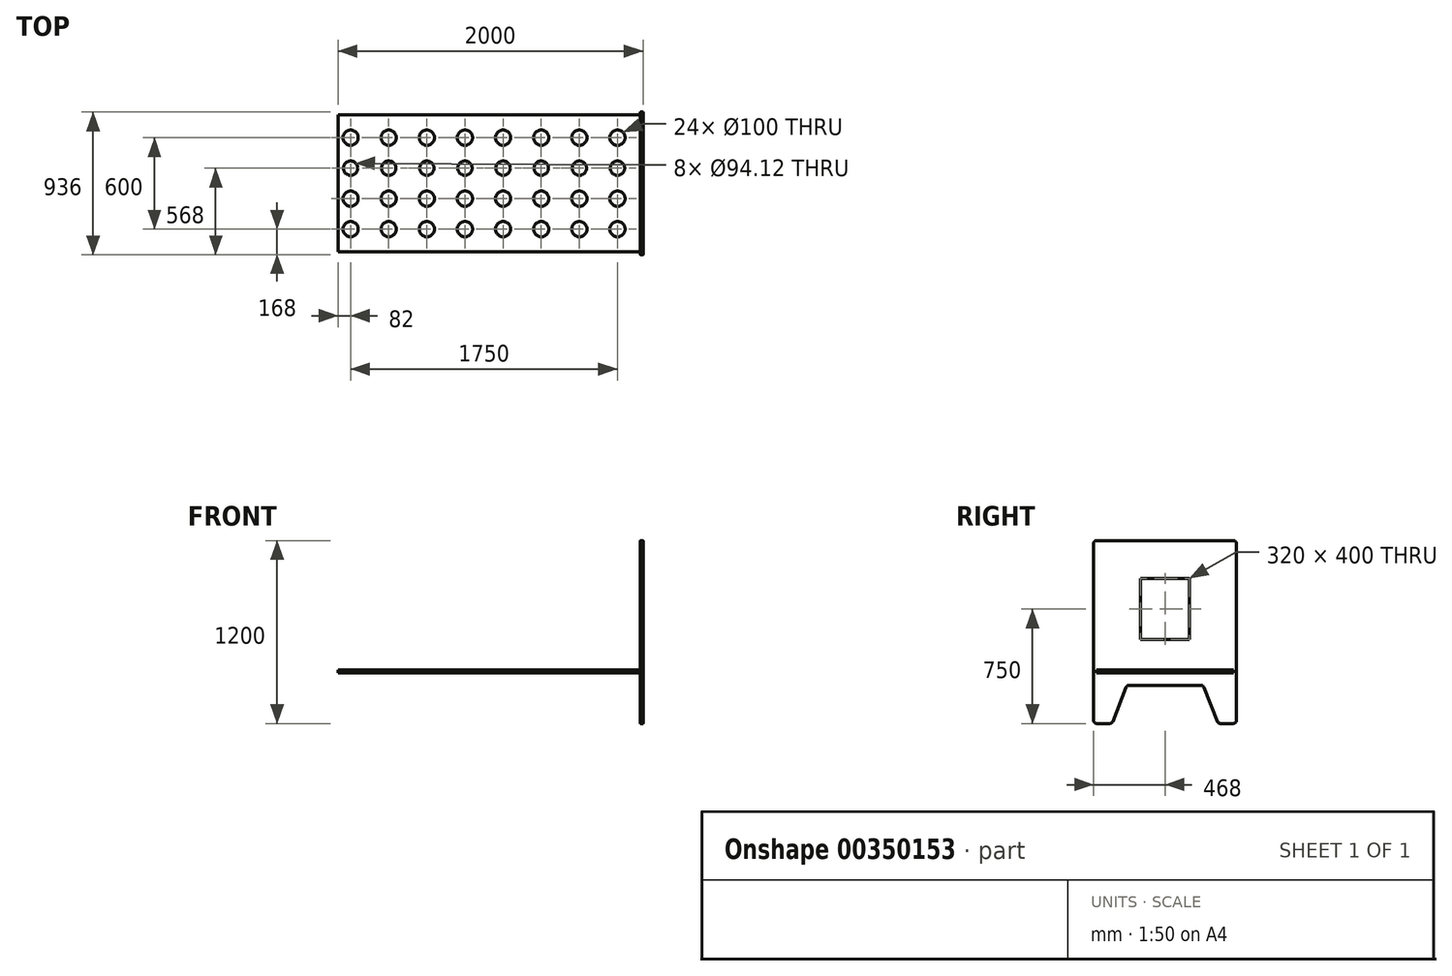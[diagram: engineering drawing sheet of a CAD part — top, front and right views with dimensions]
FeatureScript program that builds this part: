
annotation { "Feature Type Name" : "Feature", "Feature Type Description" : "" }
export const myFeature = defineFeature(function(context is Context, id is Id, definition is map)
    precondition{}
    {
        {
            var Q0;
            Q0=qCreatedBy(makeId("Right.planeOp"),FACE);
            var sketch = newSketch(context, id + "F0", { "sketchPlane" : qUnion([Q0])});
            skLineSegment(sketch, "E0.bottom", {"start": v(-468, 600) * mm, "end": v(468, 600) * mm});
            skLineSegment(sketch, "E0.top", {"start": v(-468, -600) * mm, "end": v(-348, -600) * mm});
            skLineSegment(sketch, "E0.left", {"start": v(-468, 600) * mm, "end": v(-468, -600) * mm});
            skLineSegment(sketch, "E0.right", {"start": v(468, 600) * mm, "end": v(468, -600) * mm});
            skPoint(sketch, "E0.middle", {"position": v(0, 0) * mm});
            skLineSegment(sketch, "E1", {"start": v(-348, -600) * mm, "end": v(-250, -350) * mm});
            skLineSegment(sketch, "E2", {"start": v(-250, -350) * mm, "end": v(250, -350) * mm});
            skLineSegment(sketch, "E3", {"start": v(250, -350) * mm, "end": v(348, -600) * mm});
            skLineSegment(sketch, "E4.trimOffspring", {"start": v(348, -600) * mm, "end": v(468, -600) * mm});
            skLineSegment(sketch, "E5.bottom", {"start": v(-160, 350) * mm, "end": v(160, 350) * mm});
            skLineSegment(sketch, "E5.top", {"start": v(-160, -50) * mm, "end": v(160, -50) * mm});
            skLineSegment(sketch, "E5.left", {"start": v(-160, 350) * mm, "end": v(-160, -50) * mm});
            skLineSegment(sketch, "E5.right", {"start": v(160, 350) * mm, "end": v(160, -50) * mm});
            skPoint(sketch, "E5.middle", {"position": v(0, 150) * mm});
            skSolve(sketch);
        }
        {
            var Q0;
            Q0=makeQuery(id+"F0.imprint","IMPRINT",FACE,{"disambiguationData":[TD([[makeQuery(id+"F0.imprint","IMPRINT",EDGE,{"derivedFrom":sQuery(id+"F0.wireOp",EDGE,"E0.bottom")}),-1.0]])]});
            extrude(context, id + "F1", {"entities" : qUnion([Q0]), "depth" : 18 * mm});
        }
        {
            var Q0;
            Q0=makeQuery(id+"F1.opExtrude","SWEPT_EDGE",EDGE,{"disambiguationData":[OSD([sQuery(id+"F0.wireOp",EDGE,"E0.bottom"),sQuery(id+"F0.wireOp",EDGE,"E0.left")])]});
            var Q1;
            Q1=makeQuery(id+"F1.opExtrude","SWEPT_EDGE",EDGE,{"disambiguationData":[OSD([sQuery(id+"F0.wireOp",EDGE,"E0.bottom"),sQuery(id+"F0.wireOp",EDGE,"E0.right")])]});
            var Q2;
            Q2=makeQuery(id+"F1.opExtrude","SWEPT_EDGE",EDGE,{"disambiguationData":[OSD([sQuery(id+"F0.wireOp",EDGE,"E0.right"),sQuery(id+"F0.wireOp",EDGE,"E4.trimOffspring")])]});
            var Q3;
            Q3=makeQuery(id+"F1.opExtrude","SWEPT_EDGE",EDGE,{"disambiguationData":[OSD([sQuery(id+"F0.wireOp",EDGE,"E3"),sQuery(id+"F0.wireOp",EDGE,"E4.trimOffspring")])]});
            var Q4;
            Q4=makeQuery(id+"F1.opExtrude","SWEPT_EDGE",EDGE,{"disambiguationData":[OSD([sQuery(id+"F0.wireOp",EDGE,"E2"),sQuery(id+"F0.wireOp",EDGE,"E3")])]});
            var Q5;
            Q5=makeQuery(id+"F1.opExtrude","SWEPT_EDGE",EDGE,{"disambiguationData":[OSD([sQuery(id+"F0.wireOp",EDGE,"E1"),sQuery(id+"F0.wireOp",EDGE,"E2")])]});
            var Q6;
            Q6=makeQuery(id+"F1.opExtrude","SWEPT_EDGE",EDGE,{"disambiguationData":[OSD([sQuery(id+"F0.wireOp",EDGE,"E0.top"),sQuery(id+"F0.wireOp",EDGE,"E1")])]});
            var Q7;
            Q7=makeQuery(id+"F1.opExtrude","SWEPT_EDGE",EDGE,{"disambiguationData":[OSD([sQuery(id+"F0.wireOp",EDGE,"E0.top"),sQuery(id+"F0.wireOp",EDGE,"E0.left")])]});
            fillet(context, id + "F2", {"entities" : qUnion([Q0, Q1, Q2, Q3, Q4, Q5, Q6, Q7]), "radius" : 20 * mm, "tangentPropagation" : true, "allowEdgeOverflow" : false});
        }
        {
            var Q0;
            Q0=makeQuery(id+"F1.opExtrude","SWEPT_FACE",FACE,{"disambiguationData":[OSD([sQuery(id+"F0.wireOp",EDGE,"E0.top")])]});
            cPlane(context, id + "F3", {"entities" : qUnion([Q0]), "cplaneType" : CPlaneType.OFFSET, "offset" : 350 * mm, "oppositeDirection" : true, "width" : 150 * mm, "height" : 150 * mm});
        }
        {
            var Q0;
            Q0=qCreatedBy(id+"F3.planeOp",FACE);
            var sketch = newSketch(context, id + "F4", { "sketchPlane" : qUnion([Q0])});
            skLineSegment(sketch, "E6.bottom", {"start": v(18, -450) * mm, "end": v(-1982, -450) * mm});
            skLineSegment(sketch, "E6.top", {"start": v(18, 450) * mm, "end": v(-1982, 450) * mm});
            skLineSegment(sketch, "E6.left", {"start": v(18, -467) * mm, "end": v(18, 450) * mm});
            skLineSegment(sketch, "E6.right", {"start": v(-1982, -450) * mm, "end": v(-1982, 450) * mm});
            skSolve(sketch);
        }
        {
            var Q0;
            {var subQ1=sQuery(id+"F4.wireOp",EDGE,"E6.bottom");Q0=makeQuery(id+"F4.imprint","IMPRINT",FACE,{"disambiguationData":[TD([[makeQuery(id+"F4.imprint","IMPRINT",EDGE,{"derivedFrom":subQ1}),-1.0]])]});}
            extrude(context, id + "F5", {"entities" : qUnion([Q0]), "depth" : 18 * mm});
        }
        {
            var Q0;
            Q0=makeQuery(id+"F5.opExtrude","CAP_FACE",FACE,{"disambiguationData":[OSD([sQuery(id+"F4.wireOp",EDGE,"E6.bottom"),sQuery(id+"F4.wireOp",EDGE,"E6.top"),sQuery(id+"F4.wireOp",EDGE,"E6.left"),sQuery(id+"F4.wireOp",EDGE,"E6.right"),sQuery(id+"F4.wireOp",EDGE,"7a500d48-b97b-4be0-a64c-2cbb7a61c133"),sQuery(id+"F4.wireOp",EDGE,"b0f9c249-badf-43c1-8293-a4eb95998aa5"),sQuery(id+"F4.wireOp",EDGE,"0d906021-23ab-44fd-9976-5f8d93313825"),sQuery(id+"F4.wireOp",EDGE,"47525ba4-6f94-4592-9d4c-18ce72555d00.MirrorC"),sQuery(id+"F4.wireOp",EDGE,"15bf73df-98c4-4b74-8410-59200ddc40ec.MirrorC"),sQuery(id+"F4.wireOp",EDGE,"322fc480-5554-4756-95e1-b96f7ee20b08"),sQuery(id+"F4.wireOp",EDGE,"93ea4068-c4bf-4883-9696-e8a39e370fa6"),sQuery(id+"F4.wireOp",EDGE,"54f9558f-c926-47d5-8980-b86a2ec1c04c"),sQuery(id+"F4.wireOp",EDGE,"ff3a4ad1-c42f-4fbc-b32c-5896e84eb39b.MirrorC"),sQuery(id+"F4.wireOp",EDGE,"633a068a-9ad0-4a4b-b887-519b7ecf0bd2.MirrorC"),sQuery(id+"F4.wireOp",EDGE,"536dd394-f5c1-4314-b7ec-56750df8433c"),sQuery(id+"F4.wireOp",EDGE,"0725e144-6ed3-4037-8117-f233093d21dc"),sQuery(id+"F4.wireOp",EDGE,"428a5682-b10a-4727-af5d-5744b4bac8f3"),sQuery(id+"F4.wireOp",EDGE,"1382a2c6-380c-4173-989d-5f09a39a3f8c.MirrorC"),sQuery(id+"F4.wireOp",EDGE,"9337dd30-469b-419e-948b-634ee5295446.MirrorC"),sQuery(id+"F4.wireOp",EDGE,"2c6d65fd-bf62-4a98-a149-a9e7721ad441"),sQuery(id+"F4.wireOp",EDGE,"b35cde88-149b-48d9-a2b1-007c9d3909da"),sQuery(id+"F4.wireOp",EDGE,"b56d725d-6585-4a01-9f4f-1ec2faf487c5"),sQuery(id+"F4.wireOp",EDGE,"07e47333-0485-471e-863b-75affb0af1bd.MirrorC"),sQuery(id+"F4.wireOp",EDGE,"d4a841f5-fa28-4763-820d-eab9f8d623e8.MirrorC"),sQuery(id+"F4.wireOp",EDGE,"5d69db86-a93c-4114-bf39-89364029c39e"),sQuery(id+"F4.wireOp",EDGE,"f25fc33c-f923-4e76-8d7f-009e616bc665"),sQuery(id+"F4.wireOp",EDGE,"98cb44d5-18f8-4864-9217-79acb7379e41"),sQuery(id+"F4.wireOp",EDGE,"74076fce-fee6-4c2c-ab25-7746018b45a2.MirrorC"),sQuery(id+"F4.wireOp",EDGE,"f0bc35c3-569e-4950-8cee-916eb2a78f78.MirrorC")])],"isStart":true});
            var sketch = newSketch(context, id + "F6", { "sketchPlane" : qUnion([Q0])});
            skLineSegment(sketch, "E7.bottom", {"start": v(-1882, 350) * mm, "end": v(-100, 350) * mm});
            skLineSegment(sketch, "E7.top", {"start": v(-1882, -350) * mm, "end": v(-100, -350) * mm});
            skLineSegment(sketch, "E7.left", {"start": v(-1882, 350) * mm, "end": v(-1882, -350) * mm});
            skLineSegment(sketch, "E7.right", {"start": v(-100, 350) * mm, "end": v(-100, -350) * mm});
            skPoint(sketch, "E7.middle", {"position": v(-991, 0) * mm});
            skSolve(sketch);
        }
        {
            var Q0;
            {var subQ15=sQuery(id+"F6.wireOp",EDGE,"E7.left");Q0=makeQuery(id+"F6.imprint","IMPRINT",FACE,{"disambiguationData":[TD([[makeQuery(id+"F6.imprint","IMPRINT",EDGE,{"derivedFrom":subQ15}),-1.0]])]});}
            var sketch = newSketch(context, id + "F7", { "sketchPlane" : qUnion([Q0])});
            skLineSegment(sketch, "E8", {"start": v(-275, 364.18) * mm, "end": v(-275, -209.18) * mm, "construction": true});
            skCircle(sketch, "E9", {"center": v(-150, 300) * mm, "radius": 50 * mm});
            skCircle(sketch, "E10", {"center": v(-150, 100) * mm, "radius": 47.06 * mm});
            skCircle(sketch, "E11", {"center": v(-150, -100) * mm, "radius": 50 * mm});
            skCircle(sketch, "E12", {"center": v(-150, -300) * mm, "radius": 50 * mm});
            skCircle(sketch, "E13.MirrorC", {"center": v(-400, -300) * mm, "radius": 50 * mm});
            skCircle(sketch, "E14.MirrorC", {"center": v(-400, -100) * mm, "radius": 50 * mm});
            skCircle(sketch, "E15.MirrorC", {"center": v(-400, 300) * mm, "radius": 50 * mm});
            skCircle(sketch, "E16.MirrorC", {"center": v(-400, 100) * mm, "radius": 47.06 * mm});
            skLineSegment(sketch, "E17", {"start": v(-525, 278.59) * mm, "end": v(-525, -53.99) * mm, "construction": true});
            skCircle(sketch, "E18.MirrorC", {"center": v(-650, 100) * mm, "radius": 47.06 * mm});
            skCircle(sketch, "E19.MirrorC", {"center": v(-650, 300) * mm, "radius": 50 * mm});
            skCircle(sketch, "E20.MirrorC", {"center": v(-650, -300) * mm, "radius": 50 * mm});
            skCircle(sketch, "E21.MirrorC", {"center": v(-650, -100) * mm, "radius": 50 * mm});
            skCircle(sketch, "E22.MirrorC", {"center": v(-900, 100) * mm, "radius": 47.06 * mm});
            skCircle(sketch, "E23.MirrorC", {"center": v(-900, -300) * mm, "radius": 50 * mm});
            skCircle(sketch, "E24.MirrorC", {"center": v(-900, 300) * mm, "radius": 50 * mm});
            skCircle(sketch, "E25.MirrorC", {"center": v(-900, -100) * mm, "radius": 50 * mm});
            skLineSegment(sketch, "E26", {"start": v(-1025, 259.8) * mm, "end": v(-1025, -50.44) * mm, "construction": true});
            skCircle(sketch, "E27.MirrorC", {"center": v(-1900, -300) * mm, "radius": 50 * mm});
            skCircle(sketch, "E28.MirrorC", {"center": v(-1650, -100) * mm, "radius": 50 * mm});
            skLineSegment(sketch, "E29.MirrorCS", {"start": v(-1525, 278.59) * mm, "end": v(-1525, -53.99) * mm, "construction": true});
            skCircle(sketch, "E30.MirrorC", {"center": v(-1650, 100) * mm, "radius": 47.06 * mm});
            skCircle(sketch, "E31.MirrorC", {"center": v(-1900, -100) * mm, "radius": 50 * mm});
            skCircle(sketch, "E32.MirrorC", {"center": v(-1900, 100) * mm, "radius": 47.06 * mm});
            skCircle(sketch, "E33.MirrorC", {"center": v(-1650, 300) * mm, "radius": 50 * mm});
            skCircle(sketch, "E34.MirrorC", {"center": v(-1900, 300) * mm, "radius": 50 * mm});
            skCircle(sketch, "E35.MirrorC", {"center": v(-1150, -300) * mm, "radius": 50 * mm});
            skCircle(sketch, "E36.MirrorC", {"center": v(-1400, -100) * mm, "radius": 50 * mm});
            skCircle(sketch, "E37.MirrorC", {"center": v(-1150, 100) * mm, "radius": 47.06 * mm});
            skCircle(sketch, "E38.MirrorC", {"center": v(-1400, 300) * mm, "radius": 50 * mm});
            skCircle(sketch, "E39.MirrorC", {"center": v(-1150, -100) * mm, "radius": 50 * mm});
            skLineSegment(sketch, "E40.MirrorCS", {"start": v(-1775, 364.18) * mm, "end": v(-1775, -209.18) * mm, "construction": true});
            skCircle(sketch, "E41.MirrorC", {"center": v(-1400, 100) * mm, "radius": 47.06 * mm});
            skCircle(sketch, "E42.MirrorC", {"center": v(-1650, -300) * mm, "radius": 50 * mm});
            skCircle(sketch, "E43.MirrorC", {"center": v(-1400, -300) * mm, "radius": 50 * mm});
            skCircle(sketch, "E44.MirrorC", {"center": v(-1150, 300) * mm, "radius": 50 * mm});
            skSolve(sketch);
        }
        {
            var Q0;
            Q0 = qSketchRegion(id + "F7", true);
            extrude(context, id + "F8", {"entities" : qUnion([Q0]), "operationType" : NewBodyOperationType.REMOVE, "oppositeDirection" : true, "depth" : 25 * mm});
        }
    });
